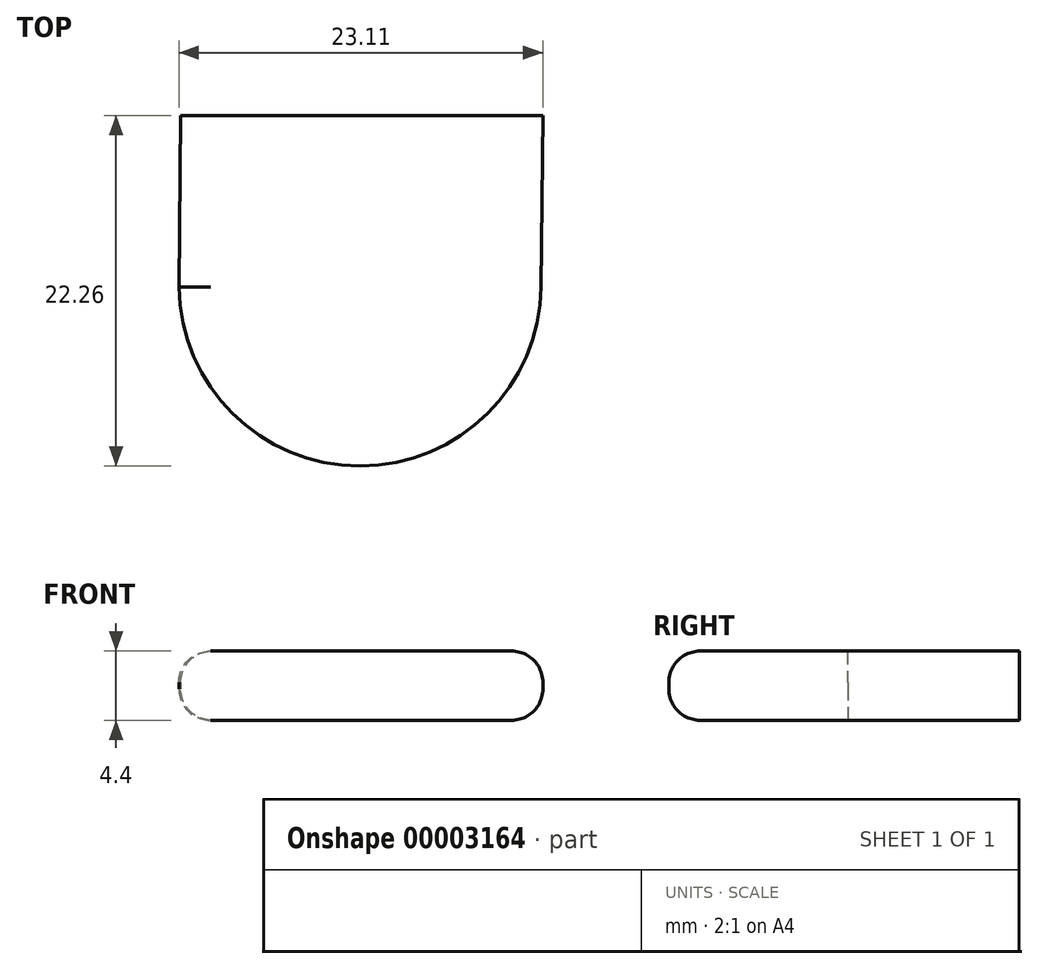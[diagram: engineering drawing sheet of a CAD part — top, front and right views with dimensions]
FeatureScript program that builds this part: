
annotation { "Feature Type Name" : "Feature", "Feature Type Description" : "" }
export const myFeature = defineFeature(function(context is Context, id is Id, definition is map)
    precondition{}
    {
        {
            var Q0;
            Q0=qCreatedBy(makeId("Top.planeOp"),FACE);
            var sketch = newSketch(context, id + "F0", { "sketchPlane" : qUnion([Q0])});
            skLineSegment(sketch, "E0", {"start": v(-53.1, 35.1) * mm, "end": v(-30.1, 35.1) * mm});
            skLineSegment(sketch, "E1", {"start": v(-30.1, 35.1) * mm, "end": v(-30.22, 24.22) * mm});
            skLineSegment(sketch, "E2", {"start": v(-53.1, 35.1) * mm, "end": v(-53.22, 24.22) * mm});
            skArc(sketch, "E3", {"start": v(-53.22, 24.22) * mm, "mid": v(-41.72, 12.84) * mm, "end": v(-30.22, 24.22) * mm});
            skLineSegment(sketch, "E4", {"start": v(-41.6, 35.1) * mm, "end": v(-41.72, 24.34) * mm, "construction": true});
            skLineSegment(sketch, "E5", {"start": v(-41.72, 24.34) * mm, "end": v(-41.72, 12.84) * mm, "construction": true});
            skSolve(sketch);
        }
        {
            var Q0;
            Q0=makeQuery(id+"F0.imprint","IMPRINT",FACE,{"disambiguationData":[TD([[makeQuery(id+"F0.imprint","IMPRINT",EDGE,{"derivedFrom":sQuery(id+"F0.wireOp",EDGE,"E0")}),-1.0]])]});
            extrude(context, id + "F1", {"entities" : qUnion([Q0]), "depth" : 4.4 * mm});
        }
        {
            var Q0;
            Q0=makeQuery(id+"F1.opExtrude","CAP_EDGE",EDGE,{"disambiguationData":[OSD([sQuery(id+"F0.wireOp",EDGE,"E3")])],"isStart":false});
            var Q1;
            Q1=makeQuery(id+"F1.opExtrude","CAP_EDGE",EDGE,{"disambiguationData":[OSD([sQuery(id+"F0.wireOp",EDGE,"E2")])],"isStart":false});
            var Q2;
            Q2=makeQuery(id+"F1.opExtrude","CAP_EDGE",EDGE,{"disambiguationData":[OSD([sQuery(id+"F0.wireOp",EDGE,"E3")])],"isStart":true});
            var Q3;
            Q3=makeQuery(id+"F1.opExtrude","CAP_EDGE",EDGE,{"disambiguationData":[OSD([sQuery(id+"F0.wireOp",EDGE,"E2")])],"isStart":true});
            var Q4;
            Q4=makeQuery(id+"F1.opExtrude","CAP_EDGE",EDGE,{"disambiguationData":[OSD([sQuery(id+"F0.wireOp",EDGE,"E1")])],"isStart":true});
            var Q5;
            Q5=makeQuery(id+"F1.opExtrude","CAP_EDGE",EDGE,{"disambiguationData":[OSD([sQuery(id+"F0.wireOp",EDGE,"E1")])],"isStart":false});
            fillet(context, id + "F2", {"entities" : qUnion([Q0, Q1, Q2, Q3, Q4, Q5]), "radius" : 2 * mm, "tangentPropagation" : true, "allowEdgeOverflow" : false});
        }
    });
